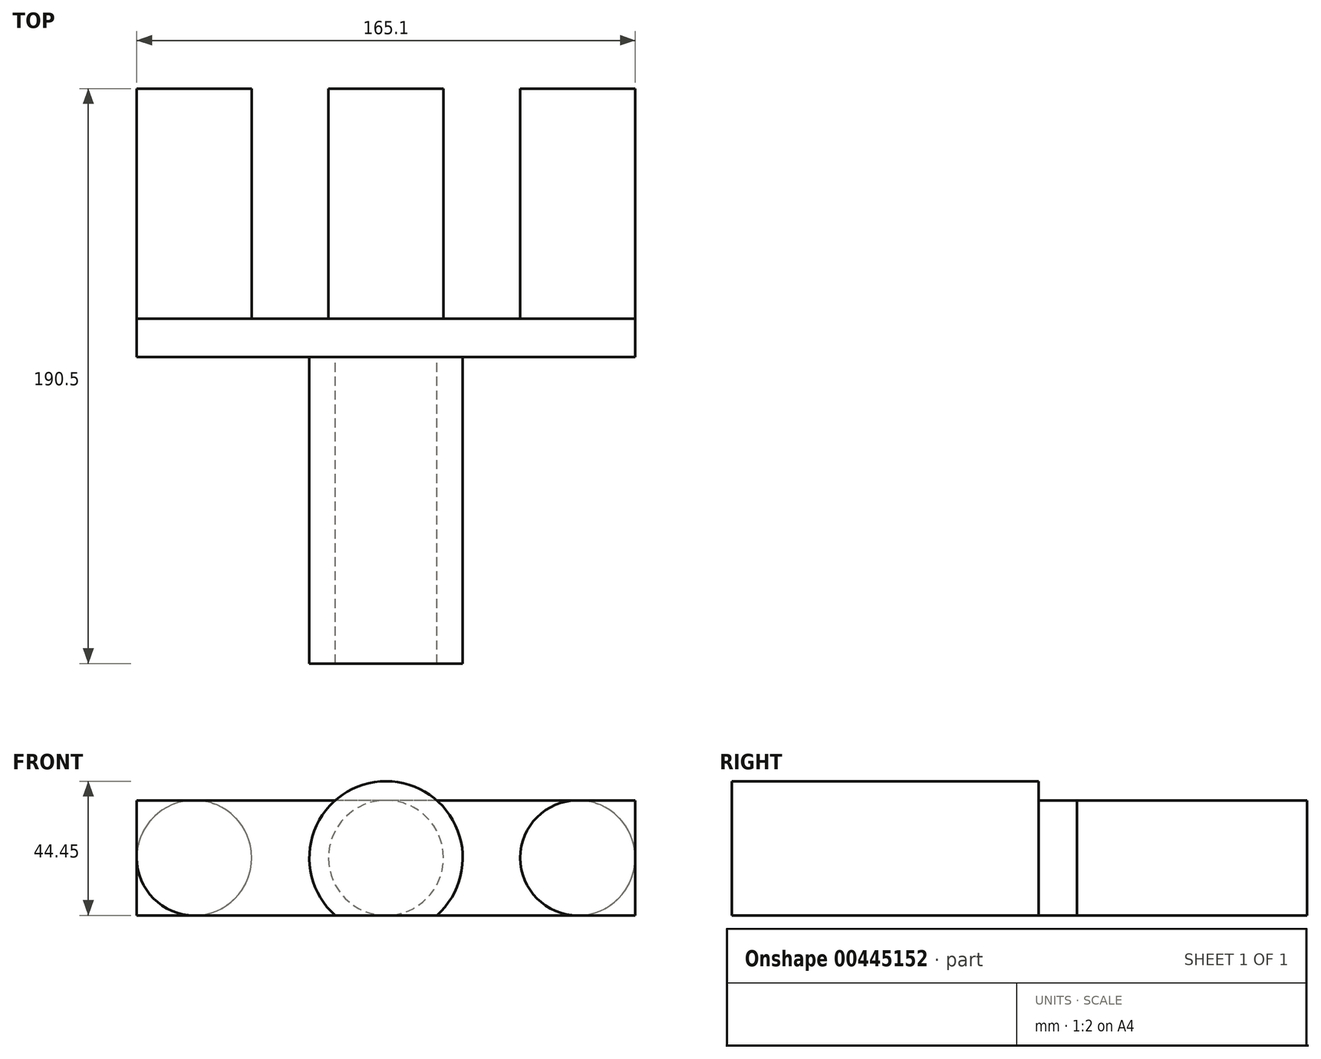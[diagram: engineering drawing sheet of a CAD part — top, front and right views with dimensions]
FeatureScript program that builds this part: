
annotation { "Feature Type Name" : "Feature", "Feature Type Description" : "" }
export const myFeature = defineFeature(function(context is Context, id is Id, definition is map)
    precondition{}
    {
        {
            var Q0;
            Q0=qCreatedBy(makeId("Front.planeOp"),FACE);
            var sketch = newSketch(context, id + "F0", { "sketchPlane" : qUnion([Q0])});
            skCircle(sketch, "E0", {"center": v(0, 0) * mm, "radius": 19.05 * mm});
            skLineSegment(sketch, "E1", {"start": v(-19.05, 0) * mm, "end": v(-63.5, 0) * mm});
            skLineSegment(sketch, "E2", {"start": v(19.05, 0) * mm, "end": v(63.5, 0) * mm});
            skCircle(sketch, "E3", {"center": v(-63.5, 0) * mm, "radius": 19.05 * mm});
            skCircle(sketch, "E4", {"center": v(63.5, 0) * mm, "radius": 19.05 * mm});
            skSolve(sketch);
        }
        {
            var Q0;
            Q0=makeQuery(id+"F0.imprint","IMPRINT",FACE,{"disambiguationData":[TD([[makeQuery(id+"F0.imprint","IMPRINT",EDGE,{"derivedFrom":sQuery(id+"F0.wireOp",EDGE,"E3")}),1.0]])]});
            var Q1;
            {var subQ0=sQuery(id+"F0.wireOp",EDGE,"E0");var subQ1=makeQuery(id+"F0.imprint","IMPRINT",VERTEX,{"disambiguationData":[OD(0.0)],"derivedFrom":subQ0});Q1=makeQuery(id+"F0.imprint","IMPRINT",FACE,{"disambiguationData":[TD([[makeQuery(id+"F0.imprint","IMPRINT",EDGE,{"disambiguationData":[TD([[subQ1,1.0]])],"derivedFrom":subQ0}),1.0]])]});}
            var Q2;
            Q2=makeQuery(id+"F0.imprint","IMPRINT",FACE,{"disambiguationData":[TD([[makeQuery(id+"F0.imprint","IMPRINT",EDGE,{"derivedFrom":sQuery(id+"F0.wireOp",EDGE,"E4")}),1.0]])]});
            extrude(context, id + "F1", {"entities" : qUnion([Q0, Q1, Q2]), "depth" : 76.2 * mm});
        }
        {
            var Q0;
            Q0=makeQuery(id+"F1.opExtrude","CAP_FACE",FACE,{"disambiguationData":[OSD([sQuery(id+"F0.wireOp",EDGE,"E0")])],"isStart":false});
            var sketch = newSketch(context, id + "F2", { "sketchPlane" : qUnion([Q0])});
            skLineSegment(sketch, "E5.bottom", {"start": v(82.55, 19.05) * mm, "end": v(-82.55, 19.05) * mm});
            skLineSegment(sketch, "E5.top", {"start": v(82.55, -19.05) * mm, "end": v(-82.55, -19.05) * mm});
            skLineSegment(sketch, "E5.left", {"start": v(82.55, 19.05) * mm, "end": v(82.55, -19.05) * mm});
            skLineSegment(sketch, "E5.right", {"start": v(-82.55, 19.05) * mm, "end": v(-82.55, -19.05) * mm});
            skPoint(sketch, "E5.middle", {"position": v(0, 0) * mm});
            skSolve(sketch);
        }
        {
            var Q0;
            {var subQ0=sQuery(id+"F2.wireOp",EDGE,"E5.right");Q0=makeQuery(id+"F2.imprint","IMPRINT",FACE,{"disambiguationData":[TD([[makeQuery(id+"F2.imprint","IMPRINT",EDGE,{"derivedFrom":subQ0}),1.0]])]});}
            var Q1;
            {var subQ0=sQuery(id+"F2.wireOp",EDGE,"E5.left");Q1=makeQuery(id+"F2.imprint","IMPRINT",FACE,{"disambiguationData":[TD([[makeQuery(id+"F2.imprint","IMPRINT",EDGE,{"derivedFrom":subQ0}),-1.0]])]});}
            var Q2;
            {var subQ0=makeQuery(id+"F1.opExtrude","CAP_EDGE",EDGE,{"disambiguationData":[OSD([sQuery(id+"F0.wireOp",EDGE,"E0")])],"isStart":false});var subQ1=makeQuery(id+"F2.imprint","INTERSECT",VERTEX,{"derivedFrom":[subQ0,sQuery(id+"F2.wireOp",EDGE,"E5.bottom")]});Q2=makeQuery(id+"F2.imprint","IMPRINT",FACE,{"disambiguationData":[TD([[makeQuery(id+"F2.imprint","IMPRINT",EDGE,{"disambiguationData":[TD([[subQ1,1.0]])],"derivedFrom":subQ0}),1.0]])]});}
            extrude(context, id + "F3", {"entities" : qUnion([Q0, Q1, Q2]), "depth" : 12.7 * mm});
        }
        {
            var Q0;
            Q0=makeQuery(id+"F3.opExtrude","CAP_FACE",FACE,{"disambiguationData":[OSD([sQuery(id+"F2.wireOp",EDGE,"E5.bottom"),sQuery(id+"F2.wireOp",EDGE,"E5.top"),sQuery(id+"F2.wireOp",EDGE,"E5.left"),sQuery(id+"F2.wireOp",EDGE,"E5.right")])],"isStart":false});
            var sketch = newSketch(context, id + "F4", { "sketchPlane" : qUnion([Q0])});
            skCircle(sketch, "E6", {"center": v(0, 0) * mm, "radius": 25.4 * mm});
            skSolve(sketch);
        }
        {
            var Q0;
            {var subQ0=sQuery(id+"F4.wireOp",EDGE,"E6");var subQ1=makeQuery(id+"F3.opExtrude","CAP_EDGE",EDGE,{"disambiguationData":[OSD([sQuery(id+"F2.wireOp",EDGE,"E5.bottom")])],"isStart":false});var subQ2=makeQuery(id+"F4.imprint","INTERSECT",VERTEX,{"disambiguationData":[OD(0.0)],"derivedFrom":[subQ1,subQ0]});Q0=makeQuery(id+"F4.imprint","IMPRINT",FACE,{"disambiguationData":[TD([[makeQuery(id+"F4.imprint","IMPRINT",EDGE,{"disambiguationData":[TD([[subQ2,1.0]])],"derivedFrom":subQ0}),1.0]])]});}
            var Q1;
            {var subQ0=sQuery(id+"F4.wireOp",EDGE,"E6");var subQ1=makeQuery(id+"F3.opExtrude","CAP_EDGE",EDGE,{"disambiguationData":[OSD([sQuery(id+"F2.wireOp",EDGE,"E5.bottom")])],"isStart":false});var subQ2=makeQuery(id+"F4.imprint","INTERSECT",VERTEX,{"disambiguationData":[OD(0.0)],"derivedFrom":[subQ1,subQ0]});Q1=makeQuery(id+"F4.imprint","IMPRINT",FACE,{"disambiguationData":[TD([[makeQuery(id+"F4.imprint","IMPRINT",EDGE,{"disambiguationData":[TD([[subQ2,-1.0]])],"derivedFrom":subQ0}),1.0]])]});}
            var Q2;
            {var subQ0=sQuery(id+"F4.wireOp",EDGE,"E6");var subQ1=makeQuery(id+"F3.opExtrude","CAP_EDGE",EDGE,{"disambiguationData":[OSD([sQuery(id+"F2.wireOp",EDGE,"E5.top")])],"isStart":false});var subQ2=makeQuery(id+"F4.imprint","INTERSECT",VERTEX,{"disambiguationData":[OD(0.0)],"derivedFrom":[subQ1,subQ0]});Q2=makeQuery(id+"F4.imprint","IMPRINT",FACE,{"disambiguationData":[TD([[makeQuery(id+"F4.imprint","IMPRINT",EDGE,{"disambiguationData":[TD([[subQ2,-1.0]])],"derivedFrom":subQ0}),1.0]])]});}
            extrude(context, id + "F5", {"entities" : qUnion([Q0, Q1, Q2]), "operationType" : NewBodyOperationType.ADD, "depth" : 101.6 * mm});
        }
    });
